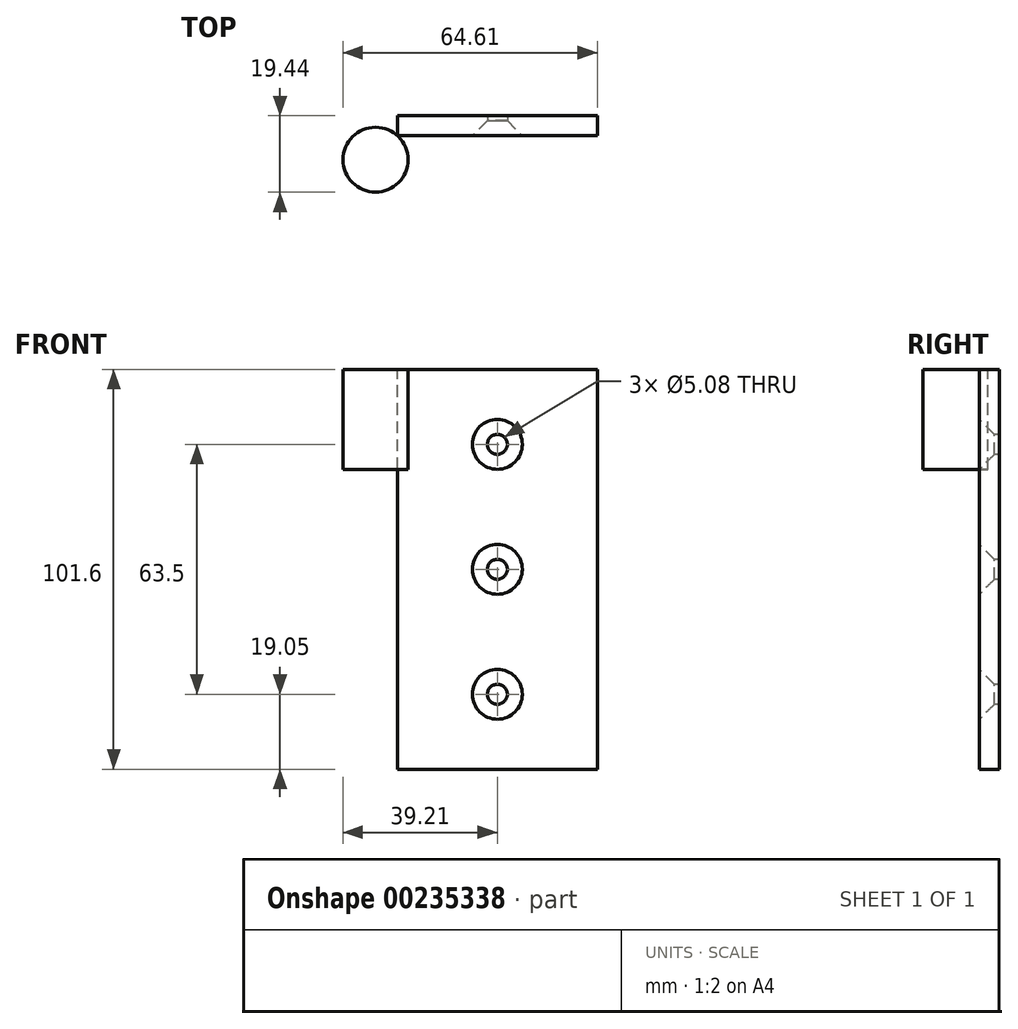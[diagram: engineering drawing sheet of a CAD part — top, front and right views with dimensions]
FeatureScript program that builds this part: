
annotation { "Feature Type Name" : "Feature", "Feature Type Description" : "" }
export const myFeature = defineFeature(function(context is Context, id is Id, definition is map)
    precondition{}
    {
        {
            var Q0;
            Q0=qCreatedBy(makeId("Front.planeOp"),FACE);
            var sketch = newSketch(context, id + "F0", { "sketchPlane" : qUnion([Q0])});
            skLineSegment(sketch, "E0.bottom", {"start": v(25.4, -50.8) * mm, "end": v(-25.4, -50.8) * mm});
            skLineSegment(sketch, "E0.top", {"start": v(25.4, 50.8) * mm, "end": v(-25.4, 50.8) * mm});
            skLineSegment(sketch, "E0.left", {"start": v(25.4, -50.8) * mm, "end": v(25.4, 50.8) * mm});
            skLineSegment(sketch, "E0.right", {"start": v(-25.4, -50.8) * mm, "end": v(-25.4, 50.8) * mm});
            skPoint(sketch, "E0.middle", {"position": v(0, 0) * mm});
            skSolve(sketch);
        }
        {
            var Q0;
            Q0 = qSketchRegion(id + "F0", true);
            extrude(context, id + "F1", {"entities" : qUnion([Q0]), "oppositeDirection" : true, "depth" : 5.08 * mm});
        }
        {
            var Q0;
            Q0=makeQuery(id+"F1.opExtrude","CAP_FACE",FACE,{"disambiguationData":[OSD([sQuery(id+"F0.wireOp",EDGE,"E0.bottom"),sQuery(id+"F0.wireOp",EDGE,"E0.top"),sQuery(id+"F0.wireOp",EDGE,"E0.left"),sQuery(id+"F0.wireOp",EDGE,"E0.right")])],"isStart":true});
            var sketch = newSketch(context, id + "F2", { "sketchPlane" : qUnion([Q0])});
            skPoint(sketch, "E1", {"position": v(0, 31.75) * mm});
            skPoint(sketch, "E2", {"position": v(0, -31.75) * mm});
            skPoint(sketch, "E3", {"position": v(0, 0) * mm});
            skSolve(sketch);
        }
        {
            var Q0;
            Q0=sQuery(id+"F2.wireOp",VERTEX,"E1");
            var Q1;
            Q1=sQuery(id+"F2.wireOp",VERTEX,"E2");
            var Q2;
            Q2=sQuery(id+"F2.wireOp",VERTEX,"E3");
            var Q3;
            Q3=makeQuery(id+"F1.opExtrude","SWEPT_BODY",BODY,{"disambiguationData":[OSD([sQuery(id+"F0.wireOp",EDGE,"E0.bottom"),sQuery(id+"F0.wireOp",EDGE,"E0.top"),sQuery(id+"F0.wireOp",EDGE,"E0.left"),sQuery(id+"F0.wireOp",EDGE,"E0.right")])]});
            hole(context, id + "F3", {"style" : HoleStyle.C_SINK, "endStyle" : HoleEndStyle.THROUGH, "holeDiameter" : 5.08 * mm, "cSinkDiameter" : 12.7 * mm, "cSinkAngle" : 90 * degree, "locations" : qUnion([Q0, Q1, Q2]), "scope" : qUnion([Q3]), "isTappedThrough" : true});
        }
        {
            var Q0;
            Q0=makeQuery(id+"F1.opExtrude","SWEPT_FACE",FACE,{"disambiguationData":[OSD([sQuery(id+"F0.wireOp",EDGE,"E0.top")])]});
            var sketch = newSketch(context, id + "F4", { "sketchPlane" : qUnion([Q0])});
            skCircle(sketch, "E4", {"center": v(-30.96, -6.1) * mm, "radius": 8.26 * mm});
            skSolve(sketch);
        }
        {
            var Q0;
            Q0 = qSketchRegion(id + "F4", true);
            extrude(context, id + "F5", {"entities" : qUnion([Q0]), "operationType" : NewBodyOperationType.ADD, "oppositeDirection" : true, "depth" : 25.4 * mm});
        }
    });
